# Revit family: Faucet-Valves_and_Controls-KOHLER-K-28139T_1
name_source: partatom
category: Plumbing Fixtures
revit_build: Autodesk Revit 2017 (Build: 20160225_1515(x64)
units: mm (PartAtom-declared; Revit-internal decimal feet)

## family parameters
Cut with Voids When Loaded = No
Host = Face
OmniClass Number = 23.27.31.00
OmniClass Title = Valves
Part Type = Normal
Room Calculation Point = No
Round Connector Dimension = Use Diameter
Shared = No

## types (1)
- NA-Stainless Steel Wire Drawing
    ADA Compliant = No
    Assembly Code = D2020
    CW Connection = Yes
    Cold Water Inlet = Cold Water Inlet
    Date Modified = 05/26/2020
    Default Elevation = 36"
    Description = Double-handle wall lavatory faucet spool stem handle spool
    Drain Included = No
    Finish = Kohler-Metal-NA-Stainless_Steel_Wire_Drawing
    Flow Rate = 0 GPM
    HW Connection = Yes
    Height = 2 1/16"
    Hot Water Inlet = Hot Water Inlet
    Length = 3 1/16"
    Manufacturer = KOHLER Co.
    MasterFormat 1995 = 154300
    MasterFormat 2004 = 22.41.39
    Material = Premium Metal Construction
    Model = K-28139T-NA
    Pressure = 116.03 psi
    Product Documentation Link = http://files.kohler.com.cn
    Product Page URL = http://www.kohler.com.cn
    URL = http://www.kohler.com.cn
    Vent Connection = No
    Waste Connection = No
    Waste Water Outlet = Waste Water Outlet
    WaterSense Certified = No
    Width = 11"

## geometry (parser evidence)
native form markers: Sweep x3
no freeform markers — native parametric forms only
